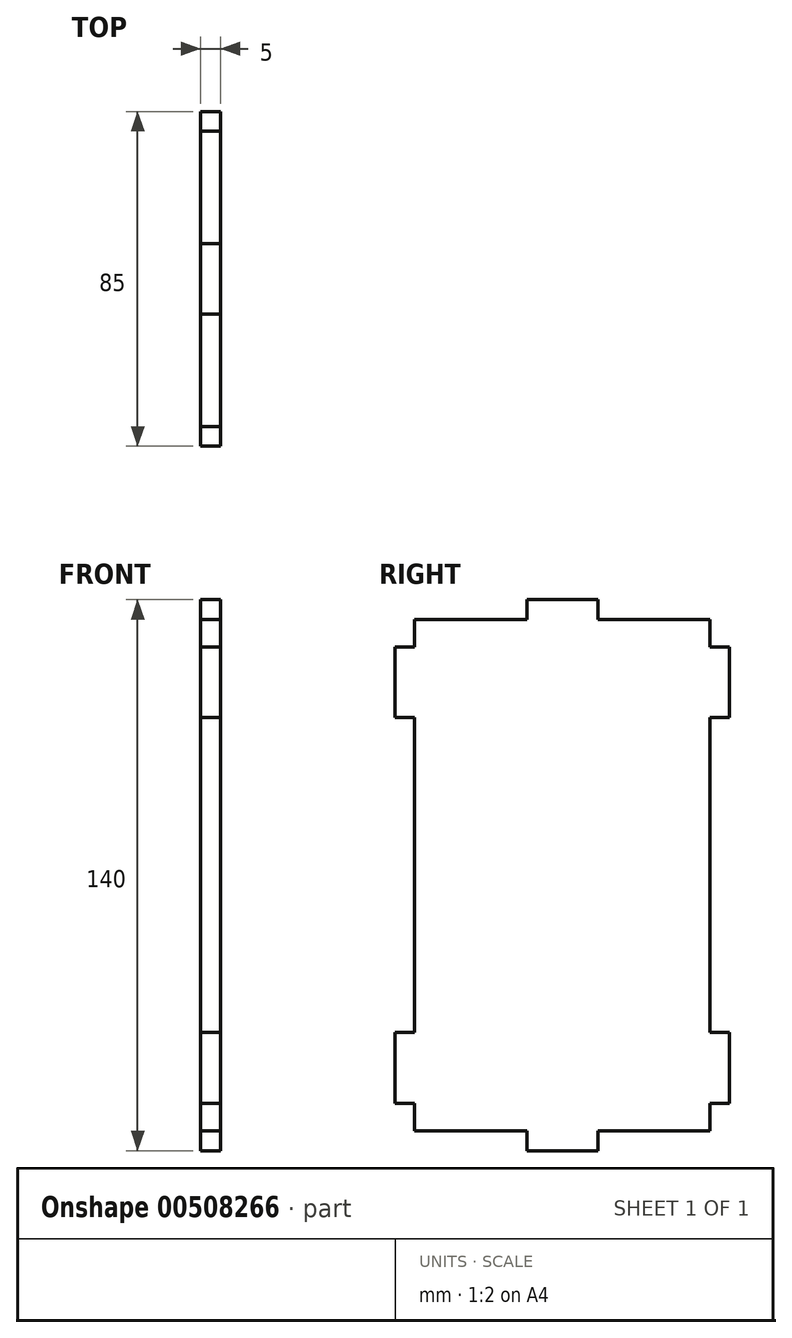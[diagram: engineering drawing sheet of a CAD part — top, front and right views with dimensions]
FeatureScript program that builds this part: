
annotation { "Feature Type Name" : "Feature", "Feature Type Description" : "" }
export const myFeature = defineFeature(function(context is Context, id is Id, definition is map)
    precondition{}
    {
        {
            var Q0;
            Q0=qCreatedBy(makeId("Right.planeOp"),FACE);
            var sketch = newSketch(context, id + "F0", { "sketchPlane" : qUnion([Q0])});
            skLineSegment(sketch, "E0.bottom", {"start": v(37.5, 65) * mm, "end": v(9, 65) * mm});
            skLineSegment(sketch, "E0.top", {"start": v(37.5, -65) * mm, "end": v(9, -65) * mm});
            skLineSegment(sketch, "E0.left", {"start": v(37.5, 65) * mm, "end": v(37.5, 58) * mm});
            skLineSegment(sketch, "E0.right", {"start": v(-37.5, 65) * mm, "end": v(-37.5, 58) * mm});
            skPoint(sketch, "E0.middle", {"position": v(0, 0) * mm});
            skLineSegment(sketch, "E1.bottom", {"start": v(37.5, 58) * mm, "end": v(42.5, 58) * mm});
            skLineSegment(sketch, "E1.top", {"start": v(37.5, 40) * mm, "end": v(42.5, 40) * mm});
            skLineSegment(sketch, "E1.right", {"start": v(42.5, 58) * mm, "end": v(42.5, 40) * mm});
            skLineSegment(sketch, "E2.bottom", {"start": v(37.5, -40) * mm, "end": v(42.5, -40) * mm});
            skLineSegment(sketch, "E2.top", {"start": v(37.5, -58) * mm, "end": v(42.5, -58) * mm});
            skLineSegment(sketch, "E2.right", {"start": v(42.5, -40) * mm, "end": v(42.5, -58) * mm});
            skLineSegment(sketch, "E3.top", {"start": v(-9, 70) * mm, "end": v(9, 70) * mm});
            skLineSegment(sketch, "E3.left", {"start": v(-9, 65) * mm, "end": v(-9, 70) * mm});
            skLineSegment(sketch, "E3.right", {"start": v(9, 65) * mm, "end": v(9, 70) * mm});
            skLineSegment(sketch, "E4.top", {"start": v(-9, -70) * mm, "end": v(9, -70) * mm});
            skLineSegment(sketch, "E4.left", {"start": v(-9, -65) * mm, "end": v(-9, -70) * mm});
            skLineSegment(sketch, "E4.right", {"start": v(9, -65) * mm, "end": v(9, -70) * mm});
            skLineSegment(sketch, "E5.trimOffspring", {"start": v(-9, 65) * mm, "end": v(-37.5, 65) * mm});
            skLineSegment(sketch, "E6.trimOffspring", {"start": v(37.5, 40) * mm, "end": v(37.5, -40) * mm});
            skLineSegment(sketch, "E7.trimOffspring", {"start": v(37.5, -58) * mm, "end": v(37.5, -65) * mm});
            skLineSegment(sketch, "E8.trimOffspring", {"start": v(-37.5, -58) * mm, "end": v(-37.5, -65) * mm});
            skLineSegment(sketch, "E9.trimOffspring", {"start": v(-9, -65) * mm, "end": v(-37.5, -65) * mm});
            skLineSegment(sketch, "E10", {"start": v(0, 0) * mm, "end": v(17.02, 0) * mm, "construction": true});
            skLineSegment(sketch, "E11", {"start": v(0, 0) * mm, "end": v(0, 15.14) * mm, "construction": true});
            skLineSegment(sketch, "E12", {"start": v(-37.5, 58) * mm, "end": v(-42.5, 58) * mm});
            skLineSegment(sketch, "E13", {"start": v(-42.5, 58) * mm, "end": v(-42.5, 40) * mm});
            skLineSegment(sketch, "E14", {"start": v(-42.5, 40) * mm, "end": v(-37.5, 40) * mm});
            skLineSegment(sketch, "E15", {"start": v(-37.5, 40) * mm, "end": v(-37.5, -40) * mm});
            skLineSegment(sketch, "E16", {"start": v(-37.5, -40) * mm, "end": v(-42.5, -40) * mm});
            skLineSegment(sketch, "E17", {"start": v(-42.5, -40) * mm, "end": v(-42.5, -58) * mm});
            skLineSegment(sketch, "E18", {"start": v(-42.5, -58) * mm, "end": v(-37.5, -58) * mm});
            skSolve(sketch);
        }
        {
            var Q0;
            Q0=makeQuery(id+"F0.imprint","IMPRINT",FACE,{"disambiguationData":[TD([[makeQuery(id+"F0.imprint","IMPRINT",EDGE,{"derivedFrom":sQuery(id+"F0.wireOp",EDGE,"E0.bottom")}),1.0]])]});
            extrude(context, id + "F1", {"entities" : qUnion([Q0]), "depth" : 5 * mm});
        }
    });
